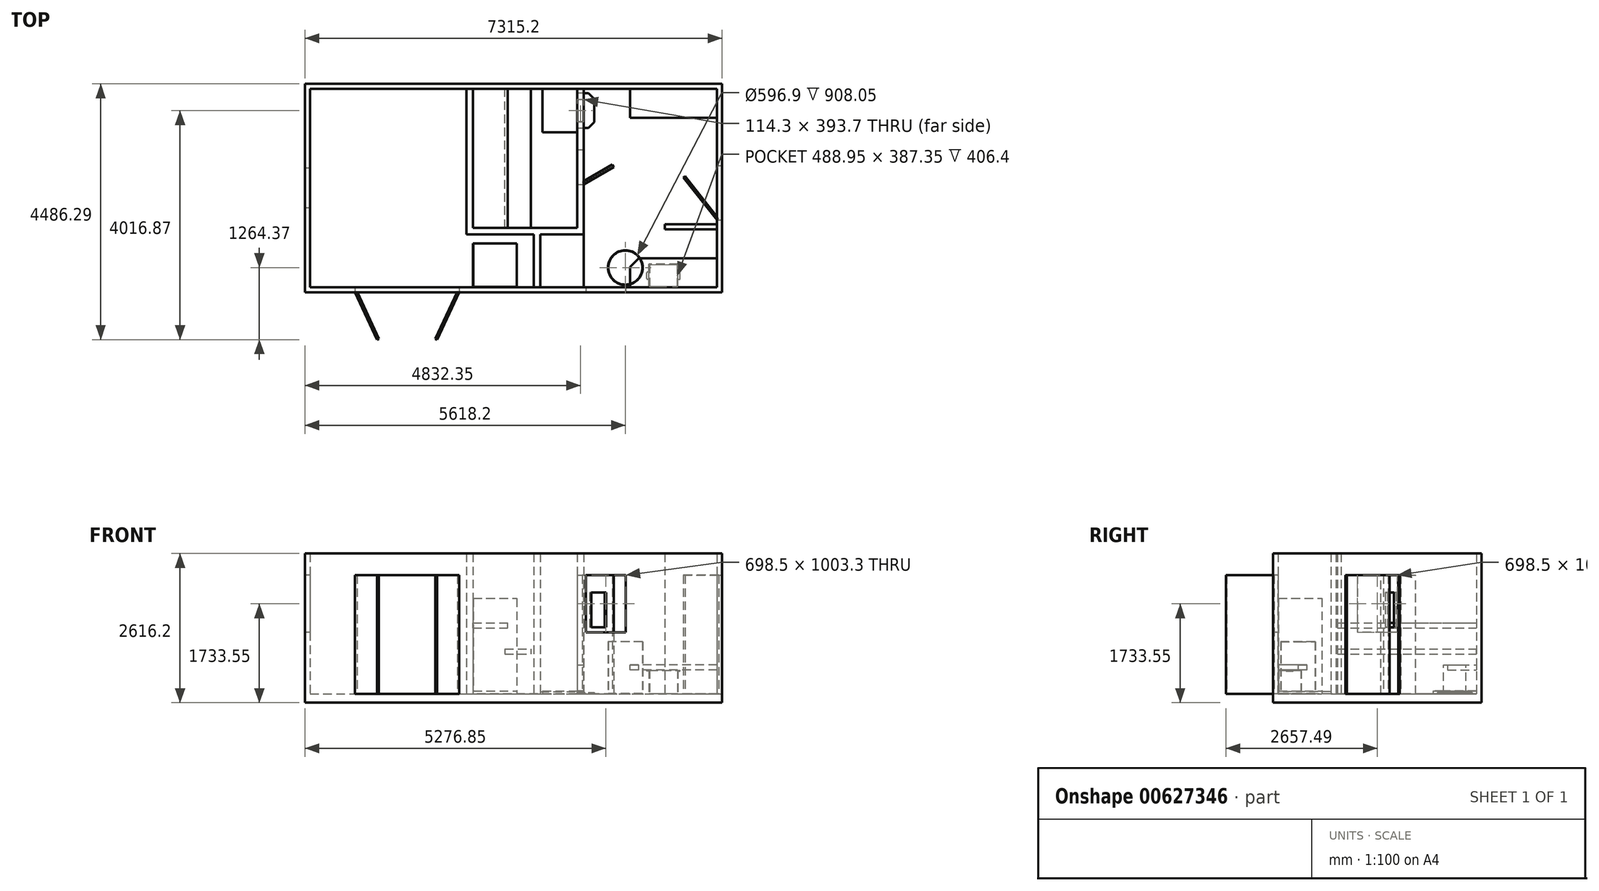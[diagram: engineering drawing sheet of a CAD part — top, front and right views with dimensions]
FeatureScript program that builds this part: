
annotation { "Feature Type Name" : "Feature", "Feature Type Description" : "" }
export const myFeature = defineFeature(function(context is Context, id is Id, definition is map)
    precondition{}
    {
        {
            var Q0;
            Q0=qCreatedBy(makeId("Top.planeOp"),FACE);
            var sketch = newSketch(context, id + "F0", { "sketchPlane" : qUnion([Q0])});
            skLineSegment(sketch, "E0.bottom", {"start": v(-3657.6, -1828.8) * mm, "end": v(3657.6, -1828.8) * mm});
            skLineSegment(sketch, "E0.top", {"start": v(-3657.6, 1828.8) * mm, "end": v(3657.6, 1828.8) * mm});
            skLineSegment(sketch, "E0.left", {"start": v(-3657.6, -1828.8) * mm, "end": v(-3657.6, 1828.8) * mm});
            skLineSegment(sketch, "E0.right", {"start": v(3657.6, -1828.8) * mm, "end": v(3657.6, 1828.8) * mm});
            skPoint(sketch, "E0.middle", {"position": v(0, 0) * mm});
            skSolve(sketch);
        }
        {
            var Q0;
            Q0=makeQuery(id+"F0.imprint","IMPRINT",FACE,{"disambiguationData":[TD([[makeQuery(id+"F0.imprint","IMPRINT",EDGE,{"derivedFrom":sQuery(id+"F0.wireOp",EDGE,"E0.bottom")}),1.0]])]});
            extrude(context, id + "F1", {"entities" : qUnion([Q0]), "depth" : 152.4 * mm});
        }
        {
            var Q0;
            Q0=makeQuery(id+"F1.opExtrude","CAP_FACE",FACE,{"disambiguationData":[OSD([sQuery(id+"F0.wireOp",EDGE,"E0.bottom"),sQuery(id+"F0.wireOp",EDGE,"E0.top"),sQuery(id+"F0.wireOp",EDGE,"E0.left"),sQuery(id+"F0.wireOp",EDGE,"E0.right")])],"isStart":false});
            var sketch = newSketch(context, id + "F2", { "sketchPlane" : qUnion([Q0])});
            skLineSegment(sketch, "E1.0", {"start": v(-3657.6, -1828.8) * mm, "end": v(-3657.6, 1828.8) * mm});
            skLineSegment(sketch, "E1.1", {"start": v(-3657.6, 1828.8) * mm, "end": v(3657.6, 1828.8) * mm});
            skLineSegment(sketch, "E1.2", {"start": v(3657.6, -1828.8) * mm, "end": v(3657.6, 1828.8) * mm});
            skLineSegment(sketch, "E1.3", {"start": v(-3657.6, -1828.8) * mm, "end": v(3657.6, -1828.8) * mm});
            skLineSegment(sketch, "E2.bottom", {"start": v(-3568.7, 1739.9) * mm, "end": v(3568.7, 1739.9) * mm});
            skLineSegment(sketch, "E2.top", {"start": v(-3568.7, -1739.9) * mm, "end": v(3568.7, -1739.9) * mm});
            skLineSegment(sketch, "E2.left", {"start": v(-3568.7, 1739.9) * mm, "end": v(-3568.7, -1739.9) * mm});
            skLineSegment(sketch, "E2.right", {"start": v(3568.7, 1739.9) * mm, "end": v(3568.7, -1739.9) * mm});
            skLineSegment(sketch, "E3", {"start": v(3568.7, 0) * mm, "end": v(0, 0) * mm, "construction": true});
            skSolve(sketch);
        }
        {
            var Q0;
            Q0=qSketchRegion(id+"F2",true);
            extrude(context, id + "F3", {"entities" : qUnion([Q0]), "depth" : 2463.8 * mm});
        }
        {
            var Q0;
            Q0=makeQuery(id+"F3.opExtrude","SWEPT_FACE",FACE,{"disambiguationData":[OSD([sQuery(id+"F2.wireOp",EDGE,"E1.2")])]});
            var sketch = newSketch(context, id + "F4", { "sketchPlane" : qUnion([Q0])});
            skLineSegment(sketch, "E4.bottom", {"start": v(-558.8, 152.4) * mm, "end": v(393.7, 152.4) * mm});
            skLineSegment(sketch, "E4.top", {"start": v(-558.8, 2235.2) * mm, "end": v(393.7, 2235.2) * mm});
            skLineSegment(sketch, "E4.left", {"start": v(-558.8, 152.4) * mm, "end": v(-558.8, 2235.2) * mm});
            skLineSegment(sketch, "E4.right", {"start": v(393.7, 152.4) * mm, "end": v(393.7, 2235.2) * mm});
            skSolve(sketch);
        }
        {
            var Q0;
            Q0=qSketchRegion(id+"F4",true);
            extrude(context, id + "F5", {"entities" : qUnion([Q0]), "operationType" : NewBodyOperationType.REMOVE, "endBound" : BoundingType.UP_TO_NEXT, "oppositeDirection" : true, "depth" : 25.4 * mm});
        }
        {
            var Q0;
            Q0=makeQuery(id+"F3.opExtrude","SWEPT_FACE",FACE,{"disambiguationData":[OSD([sQuery(id+"F2.wireOp",EDGE,"E1.3")])]});
            var sketch = newSketch(context, id + "F6", { "sketchPlane" : qUnion([Q0])});
            skLineSegment(sketch, "E5.bottom", {"start": v(-2781.3, 152.4) * mm, "end": v(-952.5, 152.4) * mm});
            skLineSegment(sketch, "E5.top", {"start": v(-2781.3, 2235.2) * mm, "end": v(-952.5, 2235.2) * mm});
            skLineSegment(sketch, "E5.left", {"start": v(-2781.3, 152.4) * mm, "end": v(-2781.3, 2235.2) * mm});
            skLineSegment(sketch, "E5.right", {"start": v(-952.5, 152.4) * mm, "end": v(-952.5, 2235.2) * mm});
            skLineSegment(sketch, "E6.bottom", {"start": v(1270, 2235.2) * mm, "end": v(1968.5, 2235.2) * mm});
            skLineSegment(sketch, "E6.top", {"start": v(1270, 1231.9) * mm, "end": v(1968.5, 1231.9) * mm});
            skLineSegment(sketch, "E6.left", {"start": v(1270, 2235.2) * mm, "end": v(1270, 1231.9) * mm});
            skLineSegment(sketch, "E6.right", {"start": v(1968.5, 2235.2) * mm, "end": v(1968.5, 1231.9) * mm});
            skSolve(sketch);
        }
        {
            var Q0;
            Q0=qSketchRegion(id+"F6",true);
            extrude(context, id + "F7", {"entities" : qUnion([Q0]), "operationType" : NewBodyOperationType.REMOVE, "endBound" : BoundingType.UP_TO_NEXT, "oppositeDirection" : true, "depth" : 25.4 * mm});
        }
        {
            var Q0;
            Q0=makeQuery(id+"F3.opExtrude","SWEPT_FACE",FACE,{"disambiguationData":[OSD([sQuery(id+"F2.wireOp",EDGE,"E1.0")])]});
            var sketch = newSketch(context, id + "F8", { "sketchPlane" : qUnion([Q0])});
            skLineSegment(sketch, "E7.bottom", {"start": v(-349.25, 2235.2) * mm, "end": v(349.25, 2235.2) * mm});
            skLineSegment(sketch, "E7.top", {"start": v(-349.25, 1231.9) * mm, "end": v(349.25, 1231.9) * mm});
            skLineSegment(sketch, "E7.left", {"start": v(-349.25, 2235.2) * mm, "end": v(-349.25, 1231.9) * mm});
            skLineSegment(sketch, "E7.right", {"start": v(349.25, 2235.2) * mm, "end": v(349.25, 1231.9) * mm});
            skLineSegment(sketch, "E8", {"start": v(0, 2235.2) * mm, "end": v(0, 1231.9) * mm, "construction": true});
            skSolve(sketch);
        }
        {
            var Q0;
            Q0=qSketchRegion(id+"F8",true);
            extrude(context, id + "F9", {"entities" : qUnion([Q0]), "operationType" : NewBodyOperationType.REMOVE, "endBound" : BoundingType.UP_TO_NEXT, "oppositeDirection" : true, "depth" : 25.4 * mm});
        }
        {
            var Q0;
            Q0=makeQuery(id+"F1.opExtrude","CAP_FACE",FACE,{"disambiguationData":[OSD([sQuery(id+"F0.wireOp",EDGE,"E0.bottom"),sQuery(id+"F0.wireOp",EDGE,"E0.top"),sQuery(id+"F0.wireOp",EDGE,"E0.left"),sQuery(id+"F0.wireOp",EDGE,"E0.right")])],"isStart":false});
            var sketch = newSketch(context, id + "F10", { "sketchPlane" : qUnion([Q0])});
            skLineSegment(sketch, "E9.bottom", {"start": v(355.6, -1739.9) * mm, "end": v(469.9, -1739.9) * mm});
            skLineSegment(sketch, "E9.top", {"start": v(-825.5, 1739.9) * mm, "end": v(-711.2, 1739.9) * mm});
            skLineSegment(sketch, "E9.left", {"start": v(-825.5, -812.8) * mm, "end": v(-825.5, 1739.9) * mm});
            skLineSegment(sketch, "E9.right", {"start": v(-711.2, -698.5) * mm, "end": v(-711.2, 1739.9) * mm});
            skLineSegment(sketch, "E10.top", {"start": v(1117.6, 1739.9) * mm, "end": v(1231.9, 1739.9) * mm});
            skLineSegment(sketch, "E11", {"start": v(1117.6, 1739.9) * mm, "end": v(1117.6, -698.5) * mm});
            skLineSegment(sketch, "E12", {"start": v(1117.6, -698.5) * mm, "end": v(-711.2, -698.5) * mm});
            skLineSegment(sketch, "E13", {"start": v(-825.5, -812.8) * mm, "end": v(1231.9, -812.8) * mm});
            skLineSegment(sketch, "E14", {"start": v(1231.9, -812.8) * mm, "end": v(1231.9, 1739.9) * mm});
            skLineSegment(sketch, "E15", {"start": v(355.6, -1739.9) * mm, "end": v(355.6, -812.8) * mm});
            skLineSegment(sketch, "E16", {"start": v(355.6, -812.8) * mm, "end": v(469.9, -812.8) * mm});
            skLineSegment(sketch, "E17", {"start": v(469.9, -812.8) * mm, "end": v(469.9, -1739.9) * mm});
            skSolve(sketch);
        }
        {
            var Q0;
            Q0=qSketchRegion(id+"F10",true);
            var Q1;
            Q1=makeQuery(id+"F3.opExtrude","CAP_FACE",FACE,{"disambiguationData":[OSD([sQuery(id+"F2.wireOp",EDGE,"E1.0"),sQuery(id+"F2.wireOp",EDGE,"E1.1"),sQuery(id+"F2.wireOp",EDGE,"E1.2"),sQuery(id+"F2.wireOp",EDGE,"E1.3"),sQuery(id+"F2.wireOp",EDGE,"E2.bottom"),sQuery(id+"F2.wireOp",EDGE,"E2.top"),sQuery(id+"F2.wireOp",EDGE,"E2.left"),sQuery(id+"F2.wireOp",EDGE,"E2.right")])],"isStart":false});
            extrude(context, id + "F11", {"entities" : qUnion([Q0]), "endBound" : BoundingType.UP_TO_SURFACE, "endBoundEntityFace" : qUnion([Q1]), "depth" : 25.4 * mm});
        }
        {
            var Q0;
            Q0=makeQuery(id+"F1.opExtrude","CAP_FACE",FACE,{"disambiguationData":[OSD([sQuery(id+"F0.wireOp",EDGE,"E0.bottom"),sQuery(id+"F0.wireOp",EDGE,"E0.top"),sQuery(id+"F0.wireOp",EDGE,"E0.left"),sQuery(id+"F0.wireOp",EDGE,"E0.right")])],"isStart":false});
            var sketch = newSketch(context, id + "F12", { "sketchPlane" : qUnion([Q0])});
            skLineSegment(sketch, "E18.bottom", {"start": v(3568.7, -723.9) * mm, "end": v(2654.3, -723.9) * mm});
            skLineSegment(sketch, "E18.top", {"start": v(3568.7, -635) * mm, "end": v(2654.3, -635) * mm});
            skLineSegment(sketch, "E18.left", {"start": v(3568.7, -723.9) * mm, "end": v(3568.7, -635) * mm});
            skLineSegment(sketch, "E18.right", {"start": v(2654.3, -723.9) * mm, "end": v(2654.3, -635) * mm});
            skSolve(sketch);
        }
        {
            var Q0;
            Q0=qSketchRegion(id+"F12",true);
            var Q1;
            Q1=makeQuery(id+"F3.opExtrude","CAP_FACE",FACE,{"disambiguationData":[OSD([sQuery(id+"F2.wireOp",EDGE,"E1.0"),sQuery(id+"F2.wireOp",EDGE,"E1.1"),sQuery(id+"F2.wireOp",EDGE,"E1.2"),sQuery(id+"F2.wireOp",EDGE,"E1.3"),sQuery(id+"F2.wireOp",EDGE,"E2.bottom"),sQuery(id+"F2.wireOp",EDGE,"E2.top"),sQuery(id+"F2.wireOp",EDGE,"E2.left"),sQuery(id+"F2.wireOp",EDGE,"E2.right")])],"isStart":false});
            extrude(context, id + "F13", {"entities" : qUnion([Q0]), "endBound" : BoundingType.UP_TO_SURFACE, "endBoundEntityFace" : qUnion([Q1]), "depth" : 25.4 * mm});
        }
        {
            var Q0;
            Q0=makeQuery(id+"F11.opExtrude","SWEPT_FACE",FACE,{"disambiguationData":[OSD([sQuery(id+"F10.wireOp",EDGE,"E14")])]});
            var sketch = newSketch(context, id + "F14", { "sketchPlane" : qUnion([Q0])});
            skLineSegment(sketch, "E19.bottom", {"start": v(63.5, 152.4) * mm, "end": v(673.1, 152.4) * mm});
            skLineSegment(sketch, "E19.top", {"start": v(63.5, 2235.2) * mm, "end": v(673.1, 2235.2) * mm});
            skLineSegment(sketch, "E19.left", {"start": v(63.5, 152.4) * mm, "end": v(63.5, 2235.2) * mm});
            skLineSegment(sketch, "E19.right", {"start": v(673.1, 152.4) * mm, "end": v(673.1, 2235.2) * mm});
            skSolve(sketch);
        }
        {
            var Q0;
            Q0=qSketchRegion(id+"F14",true);
            extrude(context, id + "F15", {"entities" : qUnion([Q0]), "operationType" : NewBodyOperationType.REMOVE, "endBound" : BoundingType.UP_TO_NEXT, "oppositeDirection" : true, "depth" : 25.4 * mm});
        }
        {
            var Q0;
            Q0=qCreatedBy(makeId("Front.planeOp"),FACE);
            var sketch = newSketch(context, id + "F16", { "sketchPlane" : qUnion([Q0])});
            skLineSegment(sketch, "E20.bottom", {"start": v(-711.2, 1308.1) * mm, "end": v(-101.6, 1308.1) * mm});
            skLineSegment(sketch, "E20.top", {"start": v(-711.2, 1397) * mm, "end": v(-101.6, 1397) * mm});
            skLineSegment(sketch, "E20.left", {"start": v(-711.2, 1308.1) * mm, "end": v(-711.2, 1397) * mm});
            skLineSegment(sketch, "E20.right", {"start": v(-101.6, 1308.1) * mm, "end": v(-101.6, 1397) * mm});
            skSolve(sketch);
        }
        {
            var Q0;
            Q0=qSketchRegion(id+"F16",true);
            extrude(context, id + "F17", {"entities" : qUnion([Q0]), "endBound" : BoundingType.UP_TO_NEXT, "depth" : 88.9 * mm, "hasSecondDirection" : true, "secondDirectionBound" : SecondDirectionBoundingType.UP_TO_NEXT, "secondDirectionOppositeDirection" : true, "secondDirectionDepth" : 25.4 * mm, "offsetDistance" : 25.4 * mm});
        }
        {
            var Q0;
            Q0=qCreatedBy(makeId("Front.planeOp"),FACE);
            var sketch = newSketch(context, id + "F18", { "sketchPlane" : qUnion([Q0])});
            skLineSegment(sketch, "E21.bottom", {"start": v(-152.4, 939.8) * mm, "end": v(304.8, 939.8) * mm});
            skLineSegment(sketch, "E21.top", {"start": v(-152.4, 850.9) * mm, "end": v(304.8, 850.9) * mm});
            skLineSegment(sketch, "E21.left", {"start": v(-152.4, 939.8) * mm, "end": v(-152.4, 850.9) * mm});
            skLineSegment(sketch, "E21.right", {"start": v(304.8, 939.8) * mm, "end": v(304.8, 850.9) * mm});
            skSolve(sketch);
        }
        {
            var Q0;
            Q0=qSketchRegion(id+"F18",true);
            extrude(context, id + "F19", {"entities" : qUnion([Q0]), "endBound" : BoundingType.UP_TO_NEXT, "depth" : 812.8 * mm, "hasSecondDirection" : true, "secondDirectionBound" : SecondDirectionBoundingType.UP_TO_NEXT, "secondDirectionOppositeDirection" : true, "secondDirectionDepth" : 1282.7 * mm, "offsetDistance" : 25.4 * mm});
        }
        {
            var Q0;
            Q0=makeQuery(id+"F3.opExtrude","SWEPT_FACE",FACE,{"disambiguationData":[OSD([sQuery(id+"F2.wireOp",EDGE,"E2.bottom")])]});
            var sketch = newSketch(context, id + "F20", { "sketchPlane" : qUnion([Q0])});
            skLineSegment(sketch, "E22.bottom", {"start": v(3568.7, 660.4) * mm, "end": v(2044.7, 660.4) * mm});
            skLineSegment(sketch, "E22.top", {"start": v(2044.7, 571.5) * mm, "end": v(3568.7, 571.5) * mm});
            skLineSegment(sketch, "E22.left", {"start": v(3568.7, 660.4) * mm, "end": v(3568.7, 571.5) * mm});
            skLineSegment(sketch, "E22.right", {"start": v(2044.7, 660.4) * mm, "end": v(2044.7, 571.5) * mm});
            skSolve(sketch);
        }
        {
            var Q0;
            Q0=qSketchRegion(id+"F20",true);
            extrude(context, id + "F21", {"entities" : qUnion([Q0]), "depth" : 508 * mm, "offsetDistance" : 25.4 * mm});
        }
        {
            var Q0;
            Q0=makeQuery(id+"F21.opExtrude","SWEPT_FACE",FACE,{"disambiguationData":[OSD([sQuery(id+"F20.wireOp",EDGE,"E22.bottom")])]});
            var sketch = newSketch(context, id + "F22", { "sketchPlane" : qUnion([Q0])});
            skLineSegment(sketch, "E23.bottom", {"start": v(2044.7, 1231.9) * mm, "end": v(2451.1, 1231.9) * mm});
            skLineSegment(sketch, "E23.top", {"start": v(2044.7, 215.9) * mm, "end": v(2451.1, 215.9) * mm});
            skLineSegment(sketch, "E23.left", {"start": v(2044.7, 215.9) * mm, "end": v(2044.7, 1231.9) * mm});
            skLineSegment(sketch, "E23.right", {"start": v(2451.1, 215.9) * mm, "end": v(2451.1, 1231.9) * mm});
            skSolve(sketch);
        }
        {
            var Q0;
            Q0=makeQuery(id+"F1.opExtrude","CAP_FACE",FACE,{"disambiguationData":[OSD([sQuery(id+"F0.wireOp",EDGE,"E0.bottom"),sQuery(id+"F0.wireOp",EDGE,"E0.top"),sQuery(id+"F0.wireOp",EDGE,"E0.left"),sQuery(id+"F0.wireOp",EDGE,"E0.right")])],"isStart":false});
            var sketch = newSketch(context, id + "F23", { "sketchPlane" : qUnion([Q0])});
            skLineSegment(sketch, "E24", {"start": v(1206.5, 107.5) * mm, "end": v(1231.9, 63.5) * mm});
            skLineSegment(sketch, "E25", {"start": v(1231.9, 63.5) * mm, "end": v(1759.83, 368.3) * mm});
            skLineSegment(sketch, "E26", {"start": v(1759.83, 368.3) * mm, "end": v(1734.43, 412.3) * mm});
            skLineSegment(sketch, "E27", {"start": v(1734.43, 412.3) * mm, "end": v(1206.5, 107.5) * mm});
            skSolve(sketch);
        }
        {
            var Q0;
            Q0=qSketchRegion(id+"F23",true);
            extrude(context, id + "F24", {"entities" : qUnion([Q0]), "depth" : 2082.8 * mm});
        }
        {
            var Q0;
            Q0=makeQuery(id+"F1.opExtrude","CAP_FACE",FACE,{"disambiguationData":[OSD([sQuery(id+"F0.wireOp",EDGE,"E0.bottom"),sQuery(id+"F0.wireOp",EDGE,"E0.top"),sQuery(id+"F0.wireOp",EDGE,"E0.left"),sQuery(id+"F0.wireOp",EDGE,"E0.right")])],"isStart":false});
            var sketch = newSketch(context, id + "F25", { "sketchPlane" : qUnion([Q0])});
            skLineSegment(sketch, "E28", {"start": v(3568.7, -558.8) * mm, "end": v(3598.59, -535.17) * mm});
            skLineSegment(sketch, "E29", {"start": v(3598.59, -535.17) * mm, "end": v(3007.81, 211.99) * mm});
            skLineSegment(sketch, "E30", {"start": v(3007.81, 211.99) * mm, "end": v(2977.93, 188.36) * mm});
            skLineSegment(sketch, "E31", {"start": v(2977.93, 188.36) * mm, "end": v(3568.7, -558.8) * mm});
            skSolve(sketch);
        }
        {
            var Q0;
            Q0=qSketchRegion(id+"F25",true);
            extrude(context, id + "F26", {"entities" : qUnion([Q0]), "depth" : 2082.8 * mm});
        }
        {
            var Q0;
            Q0=makeQuery(id+"F1.opExtrude","CAP_FACE",FACE,{"disambiguationData":[OSD([sQuery(id+"F0.wireOp",EDGE,"E0.bottom"),sQuery(id+"F0.wireOp",EDGE,"E0.top"),sQuery(id+"F0.wireOp",EDGE,"E0.left"),sQuery(id+"F0.wireOp",EDGE,"E0.right")])],"isStart":false});
            var sketch = newSketch(context, id + "F27", { "sketchPlane" : qUnion([Q0])});
            skLineSegment(sketch, "E32", {"start": v(-711.2, -1739.9) * mm, "end": v(-711.2, -971.55) * mm});
            skLineSegment(sketch, "E33", {"start": v(-711.2, -1739.9) * mm, "end": v(57.15, -1739.9) * mm});
            skLineSegment(sketch, "E34.0", {"start": v(-704.85, -1733.55) * mm, "end": v(57.15, -1733.55) * mm});
            skLineSegment(sketch, "E34.1", {"start": v(-704.85, -1733.55) * mm, "end": v(-704.85, -971.55) * mm});
            skLineSegment(sketch, "E35", {"start": v(-711.2, -971.55) * mm, "end": v(-704.85, -971.55) * mm});
            skLineSegment(sketch, "E36", {"start": v(57.15, -1739.9) * mm, "end": v(57.15, -1733.55) * mm});
            skSolve(sketch);
        }
        {
            var Q0;
            Q0=qSketchRegion(id+"F27",true);
            extrude(context, id + "F28", {"entities" : qUnion([Q0]), "depth" : 1676.4 * mm});
        }
        {
            var Q0;
            Q0=makeQuery(id+"F1.opExtrude","CAP_FACE",FACE,{"disambiguationData":[OSD([sQuery(id+"F0.wireOp",EDGE,"E0.bottom"),sQuery(id+"F0.wireOp",EDGE,"E0.top"),sQuery(id+"F0.wireOp",EDGE,"E0.left"),sQuery(id+"F0.wireOp",EDGE,"E0.right")])],"isStart":false});
            var sketch = newSketch(context, id + "F29", { "sketchPlane" : qUnion([Q0])});
            skLineSegment(sketch, "E37.bottom", {"start": v(-711.2, -1739.9) * mm, "end": v(57.15, -1739.9) * mm});
            skLineSegment(sketch, "E37.top", {"start": v(-711.2, -971.55) * mm, "end": v(57.15, -971.55) * mm});
            skLineSegment(sketch, "E37.left", {"start": v(-711.2, -1739.9) * mm, "end": v(-711.2, -971.55) * mm});
            skLineSegment(sketch, "E37.right", {"start": v(57.15, -1739.9) * mm, "end": v(57.15, -971.55) * mm});
            skSolve(sketch);
        }
        {
            var Q0;
            Q0=qSketchRegion(id+"F29",true);
            extrude(context, id + "F30", {"entities" : qUnion([Q0]), "operationType" : NewBodyOperationType.ADD, "depth" : 50.8 * mm});
        }
        {
            var Q0;
            Q0=makeQuery(id+"F3.opExtrude","SWEPT_FACE",FACE,{"disambiguationData":[OSD([sQuery(id+"F2.wireOp",EDGE,"E2.top")])]});
            var sketch = newSketch(context, id + "F31", { "sketchPlane" : qUnion([Q0])});
            skLineSegment(sketch, "E38.bottom", {"start": v(-3568.7, 660.4) * mm, "end": v(-2044.7, 660.4) * mm});
            skLineSegment(sketch, "E38.top", {"start": v(-3568.7, 571.5) * mm, "end": v(-2044.7, 571.5) * mm});
            skLineSegment(sketch, "E38.left", {"start": v(-3568.7, 660.4) * mm, "end": v(-3568.7, 571.5) * mm});
            skLineSegment(sketch, "E38.right", {"start": v(-2044.7, 660.4) * mm, "end": v(-2044.7, 571.5) * mm});
            skSolve(sketch);
        }
        {
            var Q0;
            Q0=qSketchRegion(id+"F31",true);
            extrude(context, id + "F32", {"entities" : qUnion([Q0]), "depth" : 508 * mm, "offsetDistance" : 25.4 * mm});
        }
        {
            var Q0;
            Q0=makeQuery(id+"F32.opExtrude","SWEPT_FACE",FACE,{"disambiguationData":[OSD([sQuery(id+"F31.wireOp",EDGE,"E38.bottom")])]});
            var sketch = newSketch(context, id + "F33", { "sketchPlane" : qUnion([Q0])});
            skLineSegment(sketch, "E39", {"start": v(2044.7, -1231.9) * mm, "end": v(2044.7, -1384.3) * mm});
            skLineSegment(sketch, "E40", {"start": v(2044.7, -1384.3) * mm, "end": v(2197.1, -1231.9) * mm});
            skLineSegment(sketch, "E41", {"start": v(2197.1, -1231.9) * mm, "end": v(2044.7, -1231.9) * mm});
            skSolve(sketch);
        }
        {
            var Q0;
            Q0=qSketchRegion(id+"F33",true);
            extrude(context, id + "F34", {"entities" : qUnion([Q0]), "operationType" : NewBodyOperationType.REMOVE, "endBound" : BoundingType.UP_TO_NEXT, "oppositeDirection" : true, "depth" : 25.4 * mm});
        }
        {
            var Q0;
            Q0=makeQuery(id+"F24.opExtrude","SWEPT_FACE",FACE,{"disambiguationData":[OSD([sQuery(id+"F23.wireOp",EDGE,"E25")])]});
            var sketch = newSketch(context, id + "F35", { "sketchPlane" : qUnion([Q0])});
            skLineSegment(sketch, "E42.bottom", {"start": v(1251, 1930.4) * mm, "end": v(1555.8, 1930.4) * mm});
            skLineSegment(sketch, "E42.top", {"start": v(1251, 1320.8) * mm, "end": v(1555.8, 1320.8) * mm});
            skLineSegment(sketch, "E42.left", {"start": v(1251, 1930.4) * mm, "end": v(1251, 1320.8) * mm});
            skLineSegment(sketch, "E42.right", {"start": v(1555.8, 1930.4) * mm, "end": v(1555.8, 1320.8) * mm});
            skLineSegment(sketch, "E43", {"start": v(1403.4, 2235.2) * mm, "end": v(1403.4, 1930.4) * mm, "construction": true});
            skSolve(sketch);
        }
        {
            var Q0;
            Q0=qSketchRegion(id+"F35",true);
            extrude(context, id + "F36", {"entities" : qUnion([Q0]), "operationType" : NewBodyOperationType.REMOVE, "endBound" : BoundingType.UP_TO_NEXT, "oppositeDirection" : true, "depth" : 25.4 * mm});
        }
        {
            var Q0;
            Q0=makeQuery(id+"F1.opExtrude","CAP_FACE",FACE,{"disambiguationData":[OSD([sQuery(id+"F0.wireOp",EDGE,"E0.bottom"),sQuery(id+"F0.wireOp",EDGE,"E0.top"),sQuery(id+"F0.wireOp",EDGE,"E0.left"),sQuery(id+"F0.wireOp",EDGE,"E0.right")])],"isStart":false});
            var sketch = newSketch(context, id + "F37", { "sketchPlane" : qUnion([Q0])});
            skLineSegment(sketch, "E44", {"start": v(1117.6, 977.9) * mm, "end": v(508, 977.9) * mm});
            skLineSegment(sketch, "E45", {"start": v(508, 977.9) * mm, "end": v(508, 1739.9) * mm});
            skLineSegment(sketch, "E46", {"start": v(508, 1739.9) * mm, "end": v(1117.6, 1739.9) * mm});
            skLineSegment(sketch, "E47", {"start": v(1117.6, 1739.9) * mm, "end": v(1117.6, 1555.75) * mm});
            skLineSegment(sketch, "E48", {"start": v(1117.6, 1162.05) * mm, "end": v(1219.2, 1162.05) * mm});
            skLineSegment(sketch, "E49", {"start": v(1219.2, 1162.05) * mm, "end": v(1219.2, 1555.75) * mm});
            skLineSegment(sketch, "E50", {"start": v(1219.2, 1555.75) * mm, "end": v(1117.6, 1555.75) * mm});
            skLineSegment(sketch, "E51.trimOffspring", {"start": v(1117.6, 1162.05) * mm, "end": v(1117.6, 977.9) * mm});
            skSolve(sketch);
        }
        {
            var Q0;
            Q0=qSketchRegion(id+"F37",true);
            extrude(context, id + "F38", {"entities" : qUnion([Q0]), "depth" : 50.8 * mm});
        }
        {
            var Q0;
            Q0=makeQuery(id+"F1.opExtrude","CAP_FACE",FACE,{"disambiguationData":[OSD([sQuery(id+"F0.wireOp",EDGE,"E0.bottom"),sQuery(id+"F0.wireOp",EDGE,"E0.top"),sQuery(id+"F0.wireOp",EDGE,"E0.left"),sQuery(id+"F0.wireOp",EDGE,"E0.right")])],"isStart":false});
            var sketch = newSketch(context, id + "F39", { "sketchPlane" : qUnion([Q0])});
            skLineSegment(sketch, "E52", {"start": v(1108.07, 1056.33) * mm, "end": v(1311.27, 1056.33) * mm});
            skLineSegment(sketch, "E53", {"start": v(1311.27, 1056.33) * mm, "end": v(1412.87, 1157.93) * mm});
            skLineSegment(sketch, "E54", {"start": v(1412.87, 1157.93) * mm, "end": v(1412.87, 1564.33) * mm});
            skLineSegment(sketch, "E55", {"start": v(1412.87, 1564.33) * mm, "end": v(1311.27, 1665.93) * mm});
            skLineSegment(sketch, "E56", {"start": v(1311.27, 1665.93) * mm, "end": v(1108.07, 1665.93) * mm});
            skLineSegment(sketch, "E57", {"start": v(1108.07, 1665.93) * mm, "end": v(1108.07, 1056.33) * mm});
            skLineSegment(sketch, "E58", {"start": v(1108.07, 1361.13) * mm, "end": v(1412.87, 1361.13) * mm, "construction": true});
            skSolve(sketch);
        }
        {
            var Q0;
            Q0=qSketchRegion(id+"F39",true);
            extrude(context, id + "F40", {"entities" : qUnion([Q0]), "depth" : 25.4 * mm});
        }
        {
            var Q0;
            Q0=makeQuery(id+"F1.opExtrude","CAP_FACE",FACE,{"disambiguationData":[OSD([sQuery(id+"F0.wireOp",EDGE,"E0.bottom"),sQuery(id+"F0.wireOp",EDGE,"E0.top"),sQuery(id+"F0.wireOp",EDGE,"E0.left"),sQuery(id+"F0.wireOp",EDGE,"E0.right")])],"isStart":false});
            var sketch = newSketch(context, id + "F41", { "sketchPlane" : qUnion([Q0])});
            skLineSegment(sketch, "E59.bottom", {"start": v(2883.72, -1739.9) * mm, "end": v(2375.72, -1739.9) * mm});
            skLineSegment(sketch, "E59.top", {"start": v(2883.72, -1333.5) * mm, "end": v(2375.72, -1333.5) * mm});
            skLineSegment(sketch, "E59.left", {"start": v(2883.72, -1739.9) * mm, "end": v(2883.72, -1333.5) * mm});
            skLineSegment(sketch, "E59.right", {"start": v(2375.72, -1739.9) * mm, "end": v(2375.72, -1333.5) * mm});
            skSolve(sketch);
        }
        {
            var Q0;
            Q0=qSketchRegion(id+"F41",true);
            extrude(context, id + "F42", {"entities" : qUnion([Q0]), "depth" : 9.52 * mm});
        }
        {
            var Q0;
            Q0=makeQuery(id+"F42.opExtrude","CAP_FACE",FACE,{"disambiguationData":[OSD([sQuery(id+"F41.wireOp",EDGE,"E59.bottom"),sQuery(id+"F41.wireOp",EDGE,"E59.top"),sQuery(id+"F41.wireOp",EDGE,"E59.left"),sQuery(id+"F41.wireOp",EDGE,"E59.right")])],"isStart":false});
            var sketch = newSketch(context, id + "F43", { "sketchPlane" : qUnion([Q0])});
            skLineSegment(sketch, "E60", {"start": v(2883.72, -1739.9) * mm, "end": v(2883.72, -1333.5) * mm});
            skLineSegment(sketch, "E61", {"start": v(2883.72, -1333.5) * mm, "end": v(2375.72, -1333.5) * mm});
            skLineSegment(sketch, "E62", {"start": v(2375.72, -1333.5) * mm, "end": v(2375.72, -1739.9) * mm});
            skLineSegment(sketch, "E63", {"start": v(2375.72, -1739.9) * mm, "end": v(2883.72, -1739.9) * mm});
            skLineSegment(sketch, "E64.0", {"start": v(2385.24, -1730.38) * mm, "end": v(2874.2, -1730.38) * mm});
            skLineSegment(sketch, "E64.1", {"start": v(2385.24, -1343.02) * mm, "end": v(2385.24, -1730.38) * mm});
            skLineSegment(sketch, "E64.2", {"start": v(2874.2, -1343.02) * mm, "end": v(2385.24, -1343.02) * mm});
            skLineSegment(sketch, "E64.3", {"start": v(2874.2, -1730.38) * mm, "end": v(2874.2, -1343.02) * mm});
            skSolve(sketch);
        }
        {
            var Q0;
            Q0=qSketchRegion(id+"F43",true);
            extrude(context, id + "F44", {"entities" : qUnion([Q0]), "operationType" : NewBodyOperationType.ADD, "depth" : 406.4 * mm});
        }
        {
            var Q0;
            Q0=makeQuery(id+"F44.opExtrude","CAP_FACE",FACE,{"disambiguationData":[OSD([sQuery(id+"F43.wireOp",EDGE,"E60"),sQuery(id+"F43.wireOp",EDGE,"E61"),sQuery(id+"F43.wireOp",EDGE,"E62"),sQuery(id+"F43.wireOp",EDGE,"E63"),sQuery(id+"F43.wireOp",EDGE,"E64.0"),sQuery(id+"F43.wireOp",EDGE,"E64.1"),sQuery(id+"F43.wireOp",EDGE,"E64.2"),sQuery(id+"F43.wireOp",EDGE,"E64.3")])],"isStart":false});
            var sketch = newSketch(context, id + "F45", { "sketchPlane" : qUnion([Q0])});
            skLineSegment(sketch, "E65.bottom", {"start": v(2375.72, -1600.2) * mm, "end": v(2350.32, -1600.2) * mm});
            skLineSegment(sketch, "E65.top", {"start": v(2375.72, -1473.2) * mm, "end": v(2350.32, -1473.2) * mm});
            skLineSegment(sketch, "E65.left", {"start": v(2375.72, -1600.2) * mm, "end": v(2375.72, -1473.2) * mm});
            skLineSegment(sketch, "E65.right", {"start": v(2337.62, -1587.5) * mm, "end": v(2337.62, -1485.9) * mm});
            skLineSegment(sketch, "E66.bottom", {"start": v(2883.72, -1600.2) * mm, "end": v(2909.12, -1600.2) * mm});
            skLineSegment(sketch, "E66.top", {"start": v(2883.72, -1473.2) * mm, "end": v(2909.12, -1473.2) * mm});
            skLineSegment(sketch, "E66.left", {"start": v(2883.72, -1600.2) * mm, "end": v(2883.72, -1473.2) * mm});
            skLineSegment(sketch, "E66.right", {"start": v(2921.82, -1587.5) * mm, "end": v(2921.82, -1485.9) * mm});
            skPoint(sketch, "E67.visualSharp", {"position": v(2921.82, -1600.2) * mm});
            skArc(sketch, "E67.filletArc", {"start": v(2909.12, -1600.2) * mm, "mid": v(2918.1, -1596.48) * mm, "end": v(2921.82, -1587.5) * mm});
            skPoint(sketch, "E68.visualSharp", {"position": v(2921.82, -1473.2) * mm});
            skArc(sketch, "E68.filletArc", {"start": v(2921.82, -1485.9) * mm, "mid": v(2918.1, -1476.92) * mm, "end": v(2909.12, -1473.2) * mm});
            skPoint(sketch, "E69.visualSharp", {"position": v(2337.62, -1600.2) * mm});
            skArc(sketch, "E69.filletArc", {"start": v(2337.62, -1587.5) * mm, "mid": v(2341.34, -1596.48) * mm, "end": v(2350.32, -1600.2) * mm});
            skPoint(sketch, "E70.visualSharp", {"position": v(2337.62, -1473.2) * mm});
            skArc(sketch, "E70.filletArc", {"start": v(2350.32, -1473.2) * mm, "mid": v(2341.34, -1476.92) * mm, "end": v(2337.62, -1485.9) * mm});
            skPoint(sketch, "E71", {"position": v(2874.2, -1536.7) * mm});
            skLineSegment(sketch, "E72", {"start": v(2883.72, -1536.7) * mm, "end": v(2375.72, -1536.7) * mm, "construction": true});
            skSolve(sketch);
        }
        {
            var Q0;
            Q0=qSketchRegion(id+"F45",true);
            extrude(context, id + "F46", {"entities" : qUnion([Q0]), "operationType" : NewBodyOperationType.ADD, "oppositeDirection" : true, "depth" : 12.7 * mm});
        }
        {
            var Q0;
            Q0=makeQuery(id+"F1.opExtrude","CAP_FACE",FACE,{"disambiguationData":[OSD([sQuery(id+"F0.wireOp",EDGE,"E0.bottom"),sQuery(id+"F0.wireOp",EDGE,"E0.top"),sQuery(id+"F0.wireOp",EDGE,"E0.left"),sQuery(id+"F0.wireOp",EDGE,"E0.right")])],"isStart":false});
            var sketch = newSketch(context, id + "F47", { "sketchPlane" : qUnion([Q0])});
            skLineSegment(sketch, "E73.bottom", {"start": v(3657.6, -1828.8) * mm, "end": v(3619.5, -1828.8) * mm});
            skLineSegment(sketch, "E73.top", {"start": v(3657.6, 1828.8) * mm, "end": v(3619.5, 1828.8) * mm});
            skLineSegment(sketch, "E73.left", {"start": v(3657.6, -1828.8) * mm, "end": v(3657.6, 1828.8) * mm});
            skLineSegment(sketch, "E73.right", {"start": v(3619.5, -1828.8) * mm, "end": v(3619.5, 1828.8) * mm});
            skLineSegment(sketch, "E74.1.0.0", {"start": v(3213.1, -1828.8) * mm, "end": v(3213.1, 1828.8) * mm});
            skLineSegment(sketch, "E74.1.0.1", {"start": v(3251.2, -1828.8) * mm, "end": v(3251.2, 1828.8) * mm});
            skLineSegment(sketch, "E74.2.0.0", {"start": v(2806.7, -1828.8) * mm, "end": v(2806.7, 1828.8) * mm});
            skLineSegment(sketch, "E74.2.0.1", {"start": v(2844.8, -1828.8) * mm, "end": v(2844.8, 1828.8) * mm});
            skLineSegment(sketch, "E74.3.0.0", {"start": v(2400.3, -1828.8) * mm, "end": v(2400.3, 1828.8) * mm});
            skLineSegment(sketch, "E74.3.0.1", {"start": v(2438.4, -1828.8) * mm, "end": v(2438.4, 1828.8) * mm});
            skLineSegment(sketch, "E74.4.0.0", {"start": v(1993.9, -1828.8) * mm, "end": v(1993.9, 1828.8) * mm});
            skLineSegment(sketch, "E74.4.0.1", {"start": v(2032, -1828.8) * mm, "end": v(2032, 1828.8) * mm});
            skLineSegment(sketch, "E74.5.0.0", {"start": v(1587.5, -1828.8) * mm, "end": v(1587.5, 1828.8) * mm});
            skLineSegment(sketch, "E74.5.0.1", {"start": v(1625.6, -1828.8) * mm, "end": v(1625.6, 1828.8) * mm});
            skLineSegment(sketch, "E74.6.0.0", {"start": v(1181.1, -1828.8) * mm, "end": v(1181.1, 1828.8) * mm});
            skLineSegment(sketch, "E74.6.0.1", {"start": v(1219.2, -1828.8) * mm, "end": v(1219.2, 1828.8) * mm});
            skLineSegment(sketch, "E74.7.0.0", {"start": v(774.7, -1828.8) * mm, "end": v(774.7, 1828.8) * mm});
            skLineSegment(sketch, "E74.7.0.1", {"start": v(812.8, -1828.8) * mm, "end": v(812.8, 1828.8) * mm});
            skLineSegment(sketch, "E74.8.0.0", {"start": v(368.3, -1828.8) * mm, "end": v(368.3, 1828.8) * mm});
            skLineSegment(sketch, "E74.8.0.1", {"start": v(406.4, -1828.8) * mm, "end": v(406.4, 1828.8) * mm});
            skLineSegment(sketch, "E74.9.0.0", {"start": v(-38.1, -1828.8) * mm, "end": v(-38.1, 1828.8) * mm});
            skLineSegment(sketch, "E74.9.0.1", {"start": v(0, -1828.8) * mm, "end": v(0, 1828.8) * mm});
            skLineSegment(sketch, "E74.10.0.0", {"start": v(-444.5, -1828.8) * mm, "end": v(-444.5, 1828.8) * mm});
            skLineSegment(sketch, "E74.10.0.1", {"start": v(-406.4, -1828.8) * mm, "end": v(-406.4, 1828.8) * mm});
            skLineSegment(sketch, "E74.11.0.0", {"start": v(-850.9, -1828.8) * mm, "end": v(-850.9, 1828.8) * mm});
            skLineSegment(sketch, "E74.11.0.1", {"start": v(-812.8, -1828.8) * mm, "end": v(-812.8, 1828.8) * mm});
            skLineSegment(sketch, "E74.12.0.0", {"start": v(-1257.3, -1828.8) * mm, "end": v(-1257.3, 1828.8) * mm});
            skLineSegment(sketch, "E74.12.0.1", {"start": v(-1219.2, -1828.8) * mm, "end": v(-1219.2, 1828.8) * mm});
            skLineSegment(sketch, "E74.13.0.0", {"start": v(-1663.7, -1828.8) * mm, "end": v(-1663.7, 1828.8) * mm});
            skLineSegment(sketch, "E74.13.0.1", {"start": v(-1625.6, -1828.8) * mm, "end": v(-1625.6, 1828.8) * mm});
            skLineSegment(sketch, "E74.14.0.0", {"start": v(-2070.1, -1828.8) * mm, "end": v(-2070.1, 1828.8) * mm});
            skLineSegment(sketch, "E74.14.0.1", {"start": v(-2032, -1828.8) * mm, "end": v(-2032, 1828.8) * mm});
            skLineSegment(sketch, "E74.15.0.0", {"start": v(-2476.5, -1828.8) * mm, "end": v(-2476.5, 1828.8) * mm});
            skLineSegment(sketch, "E74.15.0.1", {"start": v(-2438.4, -1828.8) * mm, "end": v(-2438.4, 1828.8) * mm});
            skLineSegment(sketch, "E74.16.0.0", {"start": v(-2882.9, -1828.8) * mm, "end": v(-2882.9, 1828.8) * mm});
            skLineSegment(sketch, "E74.16.0.1", {"start": v(-2844.8, -1828.8) * mm, "end": v(-2844.8, 1828.8) * mm});
            skLineSegment(sketch, "E74.17.0.0", {"start": v(-3289.3, -1828.8) * mm, "end": v(-3289.3, 1828.8) * mm});
            skLineSegment(sketch, "E74.17.0.1", {"start": v(-3251.2, -1828.8) * mm, "end": v(-3251.2, 1828.8) * mm});
            skLineSegment(sketch, "E74.direction1", {"start": v(3619.5, -1828.8) * mm, "end": v(3213.1, -1828.8) * mm, "construction": true});
            skLineSegment(sketch, "E75.bottom", {"start": v(-3657.6, -101.6) * mm, "end": v(3657.6, -101.6) * mm});
            skLineSegment(sketch, "E75.top", {"start": v(-3657.6, 101.6) * mm, "end": v(3657.6, 101.6) * mm});
            skLineSegment(sketch, "E75.left", {"start": v(-3657.6, 101.6) * mm, "end": v(-3657.6, -101.6) * mm});
            skLineSegment(sketch, "E75.right", {"start": v(3657.6, 101.6) * mm, "end": v(3657.6, -101.6) * mm});
            skPoint(sketch, "E76", {"position": v(-3657.6, 0) * mm});
            skSolve(sketch);
        }
        {
            var Q0;
            Q0=makeQuery(id+"F1.opExtrude","CAP_FACE",FACE,{"disambiguationData":[OSD([sQuery(id+"F0.wireOp",EDGE,"E0.bottom"),sQuery(id+"F0.wireOp",EDGE,"E0.top"),sQuery(id+"F0.wireOp",EDGE,"E0.left"),sQuery(id+"F0.wireOp",EDGE,"E0.right")])],"isStart":false});
            var sketch = newSketch(context, id + "F48", { "sketchPlane" : qUnion([Q0])});
            skLineSegment(sketch, "E77", {"start": v(-2781.3, -1828.8) * mm, "end": v(-2746.77, -1812.7) * mm});
            skLineSegment(sketch, "E78", {"start": v(-2746.77, -1812.7) * mm, "end": v(-2360.25, -2641.39) * mm});
            skLineSegment(sketch, "E79", {"start": v(-2360.25, -2641.39) * mm, "end": v(-2394.78, -2657.5) * mm});
            skLineSegment(sketch, "E80", {"start": v(-2394.78, -2657.5) * mm, "end": v(-2781.3, -1828.8) * mm});
            skLineSegment(sketch, "E81", {"start": v(-952.5, -1828.8) * mm, "end": v(-987.03, -1812.7) * mm});
            skLineSegment(sketch, "E82", {"start": v(-987.03, -1812.7) * mm, "end": v(-1373.55, -2641.39) * mm});
            skLineSegment(sketch, "E83", {"start": v(-1373.55, -2641.39) * mm, "end": v(-1339.02, -2657.5) * mm});
            skLineSegment(sketch, "E84", {"start": v(-1339.02, -2657.5) * mm, "end": v(-952.5, -1828.8) * mm});
            skSolve(sketch);
        }
        {
            var Q0;
            Q0=qSketchRegion(id+"F48",true);
            extrude(context, id + "F49", {"entities" : qUnion([Q0]), "depth" : 2082.8 * mm, "offsetDistance" : 25.4 * mm});
        }
        {
            var Q0;
            {var subQ0=sQuery(id+"F47.wireOp",EDGE,"E74.4.0.0");var subQ1=makeQuery(id+"F1.opExtrude","CAP_EDGE",EDGE,{"disambiguationData":[OSD([sQuery(id+"F0.wireOp",EDGE,"E0.bottom")])],"isStart":false});var subQ2=makeQuery(id+"F47.imprint","INTERSECT",VERTEX,{"derivedFrom":[subQ1,subQ0]});Q0=makeQuery(id+"F47.imprint","IMPRINT",FACE,{"disambiguationData":[TD([[makeQuery(id+"F47.imprint","IMPRINT",EDGE,{"disambiguationData":[TD([[subQ2,-1.0]])],"derivedFrom":subQ0}),1.0]])]});}
            var sketch = newSketch(context, id + "F50", { "sketchPlane" : qUnion([Q0])});
            skCircle(sketch, "E85", {"center": v(1960.6, -1393.12) * mm, "radius": 304.8 * mm});
            skSolve(sketch);
        }
        {
            var Q0;
            Q0 = qSketchRegion(id + "F50", true);
            extrude(context, id + "F51", {"entities" : qUnion([Q0]), "depth" : 914.4 * mm, "offsetDistance" : 25.4 * mm});
        }
        {
            var Q0;
            Q0=makeQuery(id+"F51.opExtrude","CAP_FACE",FACE,{"disambiguationData":[OSD([sQuery(id+"F50.wireOp",EDGE,"E85")])],"isStart":false});
            shell(context, id + "F52", {"entities" : qUnion([Q0]), "thickness" : 6.35 * mm});
        }
        {
            var Q0;
            Q0=makeQuery(id+"F1.opExtrude","CAP_FACE",FACE,{"disambiguationData":[OSD([sQuery(id+"F0.wireOp",EDGE,"E0.bottom"),sQuery(id+"F0.wireOp",EDGE,"E0.top"),sQuery(id+"F0.wireOp",EDGE,"E0.left"),sQuery(id+"F0.wireOp",EDGE,"E0.right")])],"isStart":false});
            var sketch = newSketch(context, id + "F53", { "sketchPlane" : qUnion([Q0])});
            skLineSegment(sketch, "E86.bottom", {"start": v(469.9, -812.8) * mm, "end": v(1231.9, -812.8) * mm});
            skLineSegment(sketch, "E86.top", {"start": v(469.9, -1739.9) * mm, "end": v(1231.9, -1739.9) * mm});
            skLineSegment(sketch, "E86.left", {"start": v(469.9, -812.8) * mm, "end": v(469.9, -1739.9) * mm});
            skLineSegment(sketch, "E86.right", {"start": v(1231.9, -812.8) * mm, "end": v(1231.9, -1739.9) * mm});
            skSolve(sketch);
        }
        {
            var Q0;
            Q0 = qSketchRegion(id + "F53", true);
            extrude(context, id + "F54", {"entities" : qUnion([Q0]), "depth" : 38.1 * mm, "offsetDistance" : 25.4 * mm});
        }
        {
            var Q0;
            Q0=makeQuery(id+"F11.opExtrude","SWEPT_FACE",FACE,{"disambiguationData":[OSD([sQuery(id+"F10.wireOp",EDGE,"E14")])]});
            var sketch = newSketch(context, id + "F55", { "sketchPlane" : qUnion([Q0])});
            skLineSegment(sketch, "E87.bottom", {"start": v(1162.53, 152.4) * mm, "end": v(1556.23, 152.4) * mm});
            skLineSegment(sketch, "E87.top", {"start": v(1162.53, 660.4) * mm, "end": v(1556.23, 660.4) * mm});
            skLineSegment(sketch, "E87.left", {"start": v(1162.53, 152.4) * mm, "end": v(1162.53, 660.4) * mm});
            skLineSegment(sketch, "E87.right", {"start": v(1556.23, 152.4) * mm, "end": v(1556.23, 660.4) * mm});
            skSolve(sketch);
        }
        {
            var Q0;
            Q0 = qSketchRegion(id + "F55", true);
            extrude(context, id + "F56", {"entities" : qUnion([Q0]), "operationType" : NewBodyOperationType.REMOVE, "endBound" : BoundingType.UP_TO_NEXT, "oppositeDirection" : true, "depth" : 25.4 * mm, "offsetDistance" : 25.4 * mm});
        }
    });
